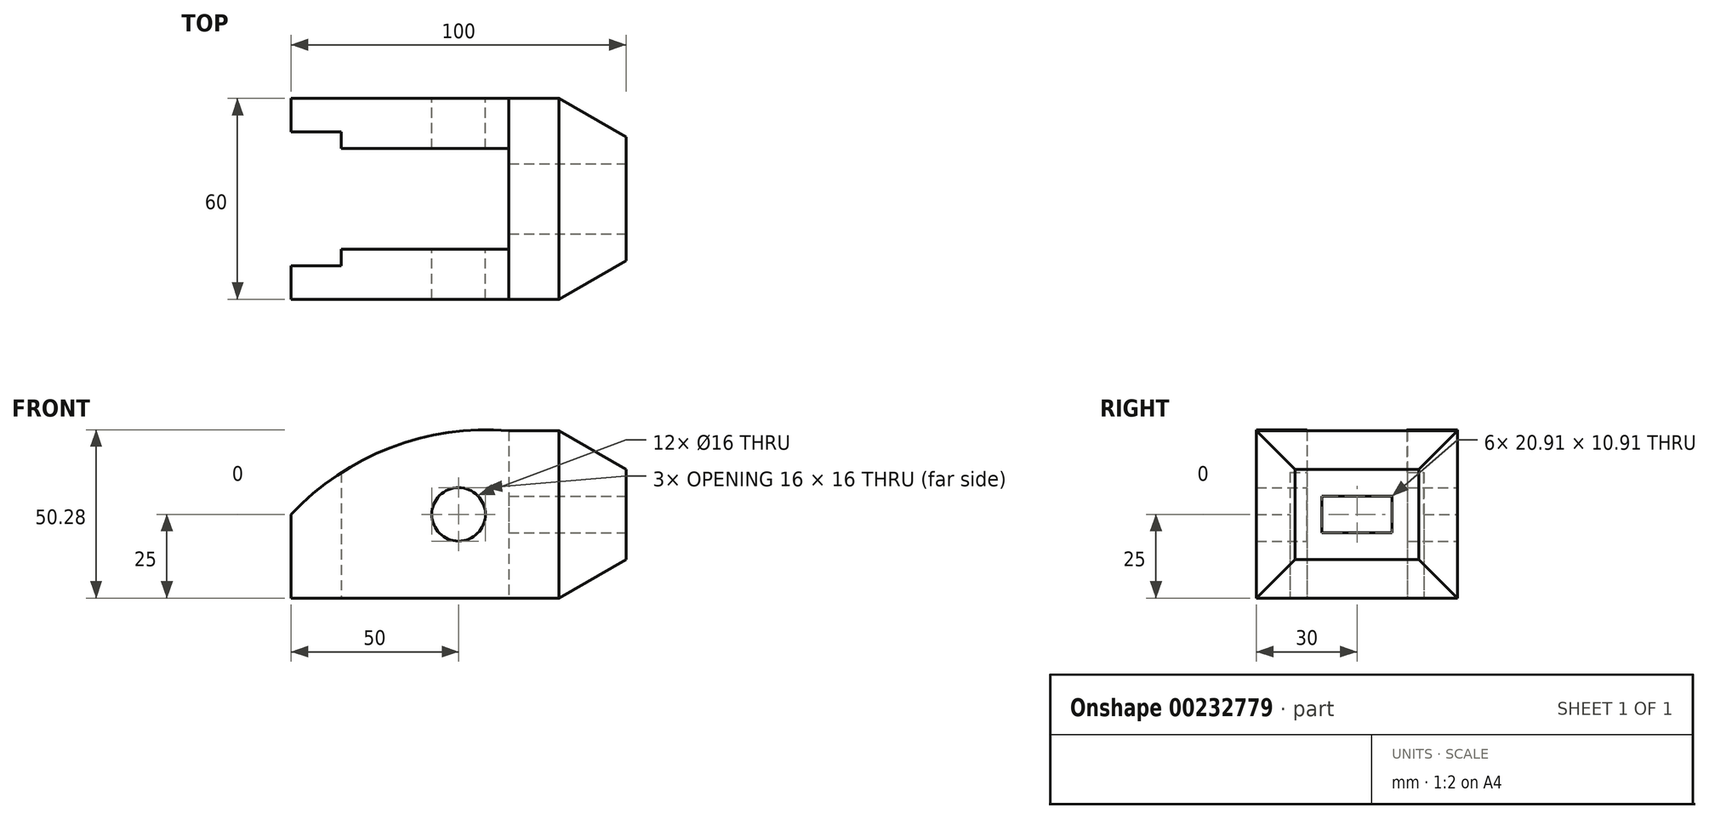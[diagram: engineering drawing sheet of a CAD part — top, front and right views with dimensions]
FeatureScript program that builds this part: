
annotation { "Feature Type Name" : "Feature", "Feature Type Description" : "" }
export const myFeature = defineFeature(function(context is Context, id is Id, definition is map)
    precondition{}
    {
        {
            var Q0;
            Q0=qCreatedBy(makeId("Front.planeOp"),FACE);
            var sketch = newSketch(context, id + "F0", { "sketchPlane" : qUnion([Q0])});
            skPoint(sketch, "E0", {"position": v(-517.79, -118.1) * mm});
            skLineSegment(sketch, "E1", {"start": v(0, 0) * mm, "end": v(-100, 0) * mm});
            skArc(sketch, "E2", {"start": v(-100, 25) * mm, "mid": v(-70.36, 44.94) * mm, "end": v(-35, 50) * mm});
            skLineSegment(sketch, "E3", {"start": v(-35, 50) * mm, "end": v(0, 50) * mm});
            skLineSegment(sketch, "E4", {"start": v(0, 50) * mm, "end": v(0, 0) * mm});
            skLineSegment(sketch, "E5", {"start": v(-100, 0) * mm, "end": v(-100, 25) * mm});
            skCircle(sketch, "E6", {"center": v(-50, 25) * mm, "radius": 8 * mm});
            skPoint(sketch, "E7", {"position": v(-50, 0) * mm});
            skSolve(sketch);
        }
        {
            var Q0;
            Q0=makeQuery(id+"F0.imprint","IMPRINT",FACE,{"disambiguationData":[TD([[makeQuery(id+"F0.imprint","IMPRINT",EDGE,{"derivedFrom":sQuery(id+"F0.wireOp",EDGE,"E1")}),-1.0]])]});
            extrude(context, id + "F1", {"entities" : qUnion([Q0]), "depth" : 60 * mm});
        }
        {
            var Q0;
            Q0=qCreatedBy(makeId("Top.planeOp"),FACE);
            var sketch = newSketch(context, id + "F2", { "sketchPlane" : qUnion([Q0])});
            skLineSegment(sketch, "E8.0.0", {"start": v(-35, 0) * mm, "end": v(-100, 0) * mm, "construction": true});
            skLineSegment(sketch, "E8.0.1", {"start": v(-100, 0) * mm, "end": v(-100, -60) * mm, "construction": true});
            skLineSegment(sketch, "E8.0.2", {"start": v(-100, -60) * mm, "end": v(-35, -60) * mm, "construction": true});
            skLineSegment(sketch, "E8.0.3", {"start": v(-35, -60) * mm, "end": v(-35, 0) * mm, "construction": true});
            skLineSegment(sketch, "E9.0.1", {"start": v(-35, 0) * mm, "end": v(-35, -60) * mm, "construction": true});
            skLineSegment(sketch, "E10", {"start": v(-100, -10) * mm, "end": v(-85, -10) * mm});
            skLineSegment(sketch, "E11", {"start": v(-85, -10) * mm, "end": v(-85, -15) * mm});
            skLineSegment(sketch, "E12", {"start": v(-85, -15) * mm, "end": v(-35, -15) * mm});
            skLineSegment(sketch, "E13", {"start": v(-35, -15) * mm, "end": v(-35, -45) * mm});
            skLineSegment(sketch, "E14", {"start": v(-35, -45) * mm, "end": v(-85, -45) * mm});
            skLineSegment(sketch, "E15", {"start": v(-85, -45) * mm, "end": v(-85, -50) * mm});
            skLineSegment(sketch, "E16", {"start": v(-85, -50) * mm, "end": v(-100, -50) * mm});
            skLineSegment(sketch, "E17", {"start": v(-100, -50) * mm, "end": v(-100, -10) * mm});
            skLineSegment(sketch, "E18", {"start": v(-100, -10) * mm, "end": v(-100, -50) * mm});
            skLineSegment(sketch, "E19", {"start": v(-20, 0) * mm, "end": v(0, -11.55) * mm});
            skLineSegment(sketch, "E20", {"start": v(0, -11.55) * mm, "end": v(0, 0) * mm});
            skLineSegment(sketch, "E21", {"start": v(-20, 0) * mm, "end": v(0, 0) * mm});
            skLineSegment(sketch, "E22", {"start": v(-35, -30) * mm, "end": v(28.95, -30) * mm, "construction": true});
            skLineSegment(sketch, "E23.0.0", {"start": v(0, 0) * mm, "end": v(-35, 0) * mm});
            skLineSegment(sketch, "E23.0.1", {"start": v(-35, 0) * mm, "end": v(-35, -60) * mm});
            skLineSegment(sketch, "E23.0.2", {"start": v(-35, -60) * mm, "end": v(0, -60) * mm});
            skLineSegment(sketch, "E23.0.3", {"start": v(0, -60) * mm, "end": v(0, 0) * mm});
            skLineSegment(sketch, "E24.MirrorCS", {"start": v(-20, -60) * mm, "end": v(0, -60) * mm});
            skLineSegment(sketch, "E25.MirrorCS", {"start": v(0, -48.45) * mm, "end": v(0, -60) * mm});
            skLineSegment(sketch, "E26.MirrorCS", {"start": v(-20, -60) * mm, "end": v(0, -48.45) * mm});
            skSolve(sketch);
        }
        {
            var Q0;
            Q0=makeQuery(id+"F2.imprint","IMPRINT",FACE,{"disambiguationData":[TD([[makeQuery(id+"F2.imprint","IMPRINT",EDGE,{"derivedFrom":sQuery(id+"F2.wireOp",EDGE,"E19")}),1.0]])]});
            var Q1;
            Q1=makeQuery(id+"F2.imprint","IMPRINT",FACE,{"disambiguationData":[TD([[makeQuery(id+"F2.imprint","IMPRINT",EDGE,{"derivedFrom":sQuery(id+"F2.wireOp",EDGE,"E26.MirrorCS")}),-1.0]])]});
            var Q2;
            Q2=makeQuery(id+"F2.imprint","IMPRINT",FACE,{"disambiguationData":[TD([[makeQuery(id+"F2.imprint","IMPRINT",EDGE,{"derivedFrom":sQuery(id+"F2.wireOp",EDGE,"E10")}),-1.0]])]});
            extrude(context, id + "F3", {"entities" : qUnion([Q0, Q1, Q2]), "operationType" : NewBodyOperationType.REMOVE, "endBound" : BoundingType.THROUGH_ALL, "depth" : 25 * mm});
        }
        {
            var Q0;
            Q0=makeQuery(id+"F1.opExtrude","CAP_FACE",FACE,{"disambiguationData":[OSD([sQuery(id+"F0.wireOp",EDGE,"E1"),sQuery(id+"F0.wireOp",EDGE,"E2"),sQuery(id+"F0.wireOp",EDGE,"E3"),sQuery(id+"F0.wireOp",EDGE,"E4"),sQuery(id+"F0.wireOp",EDGE,"E5"),sQuery(id+"F0.wireOp",EDGE,"E6")])],"isStart":false});
            var sketch = newSketch(context, id + "F4", { "sketchPlane" : qUnion([Q0])});
            skLineSegment(sketch, "E27.0", {"start": v(0, 0) * mm, "end": v(-20, 0) * mm});
            skLineSegment(sketch, "E28", {"start": v(-20, 0) * mm, "end": v(0, 11.55) * mm});
            skLineSegment(sketch, "E29", {"start": v(-50, 25) * mm, "end": v(14.89, 25) * mm, "construction": true});
            skPoint(sketch, "E30.orphan", {"position": v(-100, 0) * mm});
            skLineSegment(sketch, "E31.trimOffspring", {"start": v(0, 11.55) * mm, "end": v(0, 0) * mm});
            skPoint(sketch, "E32.0.start.orphan", {"position": v(0, 50) * mm});
            skPoint(sketch, "E33.0.start.orphan", {"position": v(-35, 50) * mm});
            skLineSegment(sketch, "E34.MirrorCS", {"start": v(0, 38.45) * mm, "end": v(0, 50) * mm});
            skLineSegment(sketch, "E35.MirrorCS", {"start": v(0, 50) * mm, "end": v(-20, 50) * mm});
            skLineSegment(sketch, "E36.MirrorCS", {"start": v(-20, 50) * mm, "end": v(0, 38.45) * mm});
            skSolve(sketch);
        }
        {
            var Q0;
            Q0=makeQuery(id+"F4.imprint","IMPRINT",FACE,{"disambiguationData":[TD([[makeQuery(id+"F4.imprint","IMPRINT",EDGE,{"derivedFrom":sQuery(id+"F4.wireOp",EDGE,"E34.MirrorCS")}),1.0]])]});
            var Q1;
            Q1=makeQuery(id+"F4.imprint","IMPRINT",FACE,{"disambiguationData":[TD([[makeQuery(id+"F4.imprint","IMPRINT",EDGE,{"derivedFrom":sQuery(id+"F4.wireOp",EDGE,"E27.0")}),-1.0]])]});
            extrude(context, id + "F5", {"entities" : qUnion([Q0, Q1]), "operationType" : NewBodyOperationType.REMOVE, "endBound" : BoundingType.THROUGH_ALL, "oppositeDirection" : true, "depth" : 25 * mm});
        }
        {
            var Q0;
            Q0=makeQuery(id+"F1.opExtrude","SWEPT_FACE",FACE,{"disambiguationData":[OSD([sQuery(id+"F0.wireOp",EDGE,"E4")])]});
            var sketch = newSketch(context, id + "F6", { "sketchPlane" : qUnion([Q0])});
            skLineSegment(sketch, "E37.0.0", {"start": v(-48.45, 11.55) * mm, "end": v(-11.55, 11.55) * mm});
            skLineSegment(sketch, "E37.0.1", {"start": v(-11.55, 11.55) * mm, "end": v(-11.55, 38.45) * mm});
            skLineSegment(sketch, "E37.0.2", {"start": v(-11.55, 38.45) * mm, "end": v(-48.45, 38.45) * mm});
            skLineSegment(sketch, "E37.0.3", {"start": v(-48.45, 38.45) * mm, "end": v(-48.45, 11.55) * mm});
            skLineSegment(sketch, "E38.0", {"start": v(-40.45, 19.55) * mm, "end": v(-19.55, 19.55) * mm});
            skLineSegment(sketch, "E38.1", {"start": v(-40.45, 30.45) * mm, "end": v(-40.45, 19.55) * mm});
            skLineSegment(sketch, "E38.2", {"start": v(-19.55, 30.45) * mm, "end": v(-40.45, 30.45) * mm});
            skLineSegment(sketch, "E38.3", {"start": v(-19.55, 19.55) * mm, "end": v(-19.55, 30.45) * mm});
            skSolve(sketch);
        }
        {
            var Q0;
            Q0=makeQuery(id+"F6.imprint","IMPRINT",FACE,{"disambiguationData":[TD([[makeQuery(id+"F6.imprint","IMPRINT",EDGE,{"derivedFrom":sQuery(id+"F6.wireOp",EDGE,"E38.0")}),1.0]])]});
            extrude(context, id + "F7", {"entities" : qUnion([Q0]), "operationType" : NewBodyOperationType.REMOVE, "endBound" : BoundingType.THROUGH_ALL, "oppositeDirection" : true, "depth" : 25 * mm});
        }
    });
